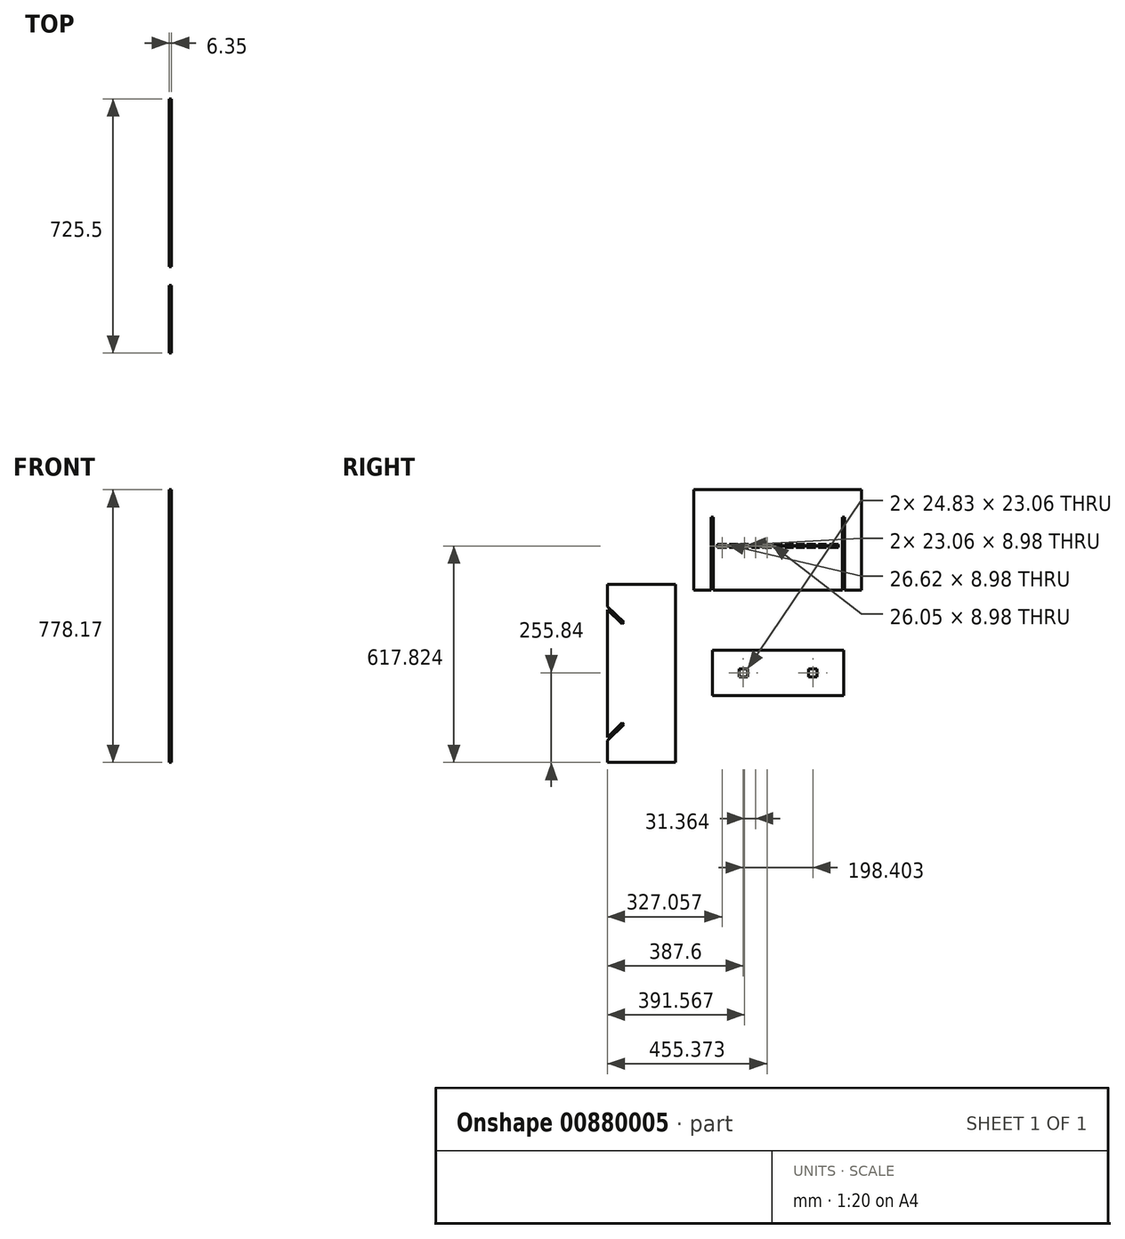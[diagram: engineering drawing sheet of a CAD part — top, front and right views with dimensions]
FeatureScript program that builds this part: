
annotation { "Feature Type Name" : "Feature", "Feature Type Description" : "" }
export const myFeature = defineFeature(function(context is Context, id is Id, definition is map)
    precondition{}
    {
        {
            var Q0;
            Q0=qCreatedBy(makeId("Right.planeOp"),FACE);
            var sketch = newSketch(context, id + "F0", { "sketchPlane" : qUnion([Q0])});
            skLineSegment(sketch, "E0.bottom", {"start": v(-465.16, 330.49) * mm, "end": v(-271.42, 330.49) * mm});
            skLineSegment(sketch, "E0.top", {"start": v(-465.16, -177.51) * mm, "end": v(-271.42, -177.51) * mm});
            skLineSegment(sketch, "E0.left", {"start": v(-465.16, 330.49) * mm, "end": v(-465.16, 267.86) * mm});
            skLineSegment(sketch, "E0.right", {"start": v(-271.42, 330.49) * mm, "end": v(-271.42, -177.51) * mm});
            skLineSegment(sketch, "E1", {"start": v(-465.16, -105.71) * mm, "end": v(-422.84, -64.86) * mm});
            skLineSegment(sketch, "E2", {"start": v(-422.84, -64.86) * mm, "end": v(-418.25, -69.62) * mm});
            skLineSegment(sketch, "E3", {"start": v(-418.25, -69.62) * mm, "end": v(-465.16, -114.9) * mm});
            skLineSegment(sketch, "E4", {"start": v(-465.16, 76.49) * mm, "end": v(-271.42, 76.49) * mm, "construction": true});
            skLineSegment(sketch, "E5.MirrorCS", {"start": v(-418.25, 222.59) * mm, "end": v(-465.16, 267.86) * mm});
            skLineSegment(sketch, "E6.MirrorCS", {"start": v(-465.16, 258.69) * mm, "end": v(-422.84, 217.84) * mm});
            skLineSegment(sketch, "E7.MirrorCS", {"start": v(-422.84, 217.84) * mm, "end": v(-418.25, 222.59) * mm});
            skLineSegment(sketch, "E8.bottom", {"start": v(-166.04, 143.36) * mm, "end": v(209.33, 143.36) * mm});
            skLineSegment(sketch, "E8.top", {"start": v(-166.04, 12.79) * mm, "end": v(209.33, 12.79) * mm});
            skLineSegment(sketch, "E8.left", {"start": v(-166.04, 143.36) * mm, "end": v(-166.04, 12.79) * mm});
            skLineSegment(sketch, "E8.right", {"start": v(209.33, 143.36) * mm, "end": v(209.33, 12.79) * mm});
            skLineSegment(sketch, "E9.bottom", {"start": v(-89.98, 89.86) * mm, "end": v(-65.14, 89.86) * mm});
            skLineSegment(sketch, "E9.top", {"start": v(-89.98, 66.8) * mm, "end": v(-65.14, 66.8) * mm});
            skLineSegment(sketch, "E9.left", {"start": v(-89.98, 89.86) * mm, "end": v(-89.98, 66.8) * mm});
            skLineSegment(sketch, "E9.right", {"start": v(-65.14, 89.86) * mm, "end": v(-65.14, 66.8) * mm});
            skLineSegment(sketch, "E10", {"start": v(21.64, 143.36) * mm, "end": v(21.64, 12.79) * mm, "construction": true});
            skLineSegment(sketch, "E11.MirrorCS", {"start": v(133.26, 89.86) * mm, "end": v(108.43, 89.86) * mm});
            skLineSegment(sketch, "E12.MirrorCS", {"start": v(133.26, 89.86) * mm, "end": v(133.26, 66.8) * mm});
            skLineSegment(sketch, "E13.MirrorCS", {"start": v(133.26, 66.8) * mm, "end": v(108.43, 66.8) * mm});
            skLineSegment(sketch, "E14.MirrorCS", {"start": v(108.43, 89.86) * mm, "end": v(108.43, 66.8) * mm});
            skLineSegment(sketch, "E15.bottom", {"start": v(-218.27, 600.66) * mm, "end": v(260.34, 600.66) * mm});
            skLineSegment(sketch, "E15.top", {"start": v(-218.27, 314.51) * mm, "end": v(-169.33, 314.51) * mm});
            skLineSegment(sketch, "E15.left", {"start": v(-218.27, 600.66) * mm, "end": v(-218.27, 314.51) * mm});
            skLineSegment(sketch, "E15.right", {"start": v(260.34, 600.66) * mm, "end": v(260.34, 314.51) * mm});
            skLineSegment(sketch, "E16.top", {"start": v(-162.72, 521.91) * mm, "end": v(-169.33, 521.91) * mm});
            skLineSegment(sketch, "E16.left", {"start": v(-162.72, 314.51) * mm, "end": v(-162.72, 521.91) * mm});
            skLineSegment(sketch, "E16.right", {"start": v(-169.33, 314.51) * mm, "end": v(-169.33, 521.91) * mm});
            skLineSegment(sketch, "E17.bottom", {"start": v(-151.41, 444.8) * mm, "end": v(-124.8, 444.8) * mm});
            skLineSegment(sketch, "E17.top", {"start": v(-151.41, 435.83) * mm, "end": v(-124.8, 435.83) * mm});
            skLineSegment(sketch, "E17.left", {"start": v(-151.41, 444.8) * mm, "end": v(-151.41, 435.83) * mm});
            skLineSegment(sketch, "E17.right", {"start": v(193.48, 444.8) * mm, "end": v(193.48, 435.83) * mm});
            skLineSegment(sketch, "E18", {"start": v(21.03, 444.8) * mm, "end": v(21.03, 435.83) * mm, "construction": true});
            skLineSegment(sketch, "E19.MirrorCS", {"start": v(204.79, 314.51) * mm, "end": v(204.79, 521.91) * mm});
            skLineSegment(sketch, "E20.MirrorCS", {"start": v(211.39, 314.51) * mm, "end": v(211.39, 521.91) * mm});
            skLineSegment(sketch, "E21.MirrorCS", {"start": v(204.79, 521.91) * mm, "end": v(211.39, 521.91) * mm});
            skLineSegment(sketch, "E22", {"start": v(21.03, 600.66) * mm, "end": v(21.03, 314.51) * mm, "construction": true});
            skLineSegment(sketch, "E23.left", {"start": v(-124.8, 444.8) * mm, "end": v(-124.8, 435.83) * mm});
            skLineSegment(sketch, "E23.right", {"start": v(-117.32, 444.8) * mm, "end": v(-117.32, 435.83) * mm});
            skLineSegment(sketch, "E24.left", {"start": v(-92.6, 444.8) * mm, "end": v(-92.6, 435.83) * mm});
            skLineSegment(sketch, "E24.right", {"start": v(-85.12, 444.8) * mm, "end": v(-85.12, 435.83) * mm});
            skLineSegment(sketch, "E25.left", {"start": v(-62.06, 444.8) * mm, "end": v(-62.06, 435.83) * mm});
            skLineSegment(sketch, "E25.right", {"start": v(-53.76, 444.8) * mm, "end": v(-53.76, 435.83) * mm});
            skLineSegment(sketch, "E26.left", {"start": v(-30.7, 444.8) * mm, "end": v(-30.7, 435.83) * mm});
            skLineSegment(sketch, "E26.right", {"start": v(-22.81, 444.8) * mm, "end": v(-22.81, 435.83) * mm});
            skLineSegment(sketch, "E27.left", {"start": v(3.24, 444.8) * mm, "end": v(3.24, 435.83) * mm});
            skLineSegment(sketch, "E27.right", {"start": v(10.14, 444.8) * mm, "end": v(10.14, 435.83) * mm});
            skLineSegment(sketch, "E28.left", {"start": v(34.07, 444.8) * mm, "end": v(34.07, 435.83) * mm});
            skLineSegment(sketch, "E28.right", {"start": v(40.98, 444.8) * mm, "end": v(40.98, 435.83) * mm});
            skLineSegment(sketch, "E29.left", {"start": v(65.24, 444.8) * mm, "end": v(65.24, 435.83) * mm});
            skLineSegment(sketch, "E29.right", {"start": v(72.92, 444.8) * mm, "end": v(72.92, 435.83) * mm});
            skLineSegment(sketch, "E30.left", {"start": v(96.84, 444.8) * mm, "end": v(96.84, 435.83) * mm});
            skLineSegment(sketch, "E30.right", {"start": v(103.24, 444.8) * mm, "end": v(103.24, 435.83) * mm});
            skLineSegment(sketch, "E31.left", {"start": v(128.95, 444.8) * mm, "end": v(128.95, 435.83) * mm});
            skLineSegment(sketch, "E31.right", {"start": v(137.02, 444.8) * mm, "end": v(137.02, 435.83) * mm});
            skLineSegment(sketch, "E32.left", {"start": v(159.68, 444.8) * mm, "end": v(159.68, 435.83) * mm});
            skLineSegment(sketch, "E32.right", {"start": v(168, 444.8) * mm, "end": v(168, 435.83) * mm});
            skLineSegment(sketch, "E33.trimOffspring", {"start": v(168, 435.83) * mm, "end": v(193.48, 435.83) * mm});
            skLineSegment(sketch, "E34.trimOffspring", {"start": v(168, 444.8) * mm, "end": v(193.48, 444.8) * mm});
            skLineSegment(sketch, "E35.trimOffspring", {"start": v(137.02, 444.8) * mm, "end": v(159.68, 444.8) * mm});
            skLineSegment(sketch, "E36.trimOffspring", {"start": v(137.02, 435.83) * mm, "end": v(159.68, 435.83) * mm});
            skLineSegment(sketch, "E37.trimOffspring", {"start": v(103.24, 435.83) * mm, "end": v(128.95, 435.83) * mm});
            skLineSegment(sketch, "E38.trimOffspring", {"start": v(103.24, 444.8) * mm, "end": v(128.95, 444.8) * mm});
            skLineSegment(sketch, "E39.trimOffspring", {"start": v(72.92, 435.83) * mm, "end": v(96.84, 435.83) * mm});
            skLineSegment(sketch, "E40.trimOffspring", {"start": v(40.98, 444.8) * mm, "end": v(65.24, 444.8) * mm});
            skLineSegment(sketch, "E41.trimOffspring", {"start": v(40.98, 435.83) * mm, "end": v(65.24, 435.83) * mm});
            skLineSegment(sketch, "E42.trimOffspring", {"start": v(72.92, 444.8) * mm, "end": v(96.84, 444.8) * mm});
            skLineSegment(sketch, "E43.trimOffspring", {"start": v(10.14, 435.83) * mm, "end": v(34.07, 435.83) * mm});
            skLineSegment(sketch, "E44.trimOffspring", {"start": v(-22.81, 435.83) * mm, "end": v(3.24, 435.83) * mm});
            skLineSegment(sketch, "E45.trimOffspring", {"start": v(-22.81, 444.8) * mm, "end": v(34.07, 444.8) * mm});
            skLineSegment(sketch, "E46.trimOffspring", {"start": v(-53.76, 444.8) * mm, "end": v(-30.7, 444.8) * mm});
            skLineSegment(sketch, "E47.trimOffspring", {"start": v(-53.76, 435.83) * mm, "end": v(-30.7, 435.83) * mm});
            skLineSegment(sketch, "E48.trimOffspring", {"start": v(-85.12, 444.8) * mm, "end": v(-62.06, 444.8) * mm});
            skLineSegment(sketch, "E49.trimOffspring", {"start": v(-85.12, 435.83) * mm, "end": v(-62.06, 435.83) * mm});
            skLineSegment(sketch, "E50.trimOffspring", {"start": v(-117.32, 444.8) * mm, "end": v(-92.6, 444.8) * mm});
            skLineSegment(sketch, "E51.trimOffspring", {"start": v(-117.32, 435.83) * mm, "end": v(-92.6, 435.83) * mm});
            skLineSegment(sketch, "E52.trimOffspring", {"start": v(-465.16, 258.69) * mm, "end": v(-465.16, -105.71) * mm});
            skLineSegment(sketch, "E53.trimOffspring", {"start": v(-465.16, -114.9) * mm, "end": v(-465.16, -177.51) * mm});
            skLineSegment(sketch, "E54.trimOffspring", {"start": v(211.39, 314.51) * mm, "end": v(260.34, 314.51) * mm});
            skLineSegment(sketch, "E55.trimOffspring", {"start": v(-162.72, 314.51) * mm, "end": v(204.79, 314.51) * mm});
            skSolve(sketch);
        }
        {
            var Q0;
            Q0 = qSketchRegion(id + "F0", true);
            extrude(context, id + "F1", {"entities" : qUnion([Q0]), "depth" : 6.35 * mm, "offsetDistance" : 25.4 * mm});
        }
    });
